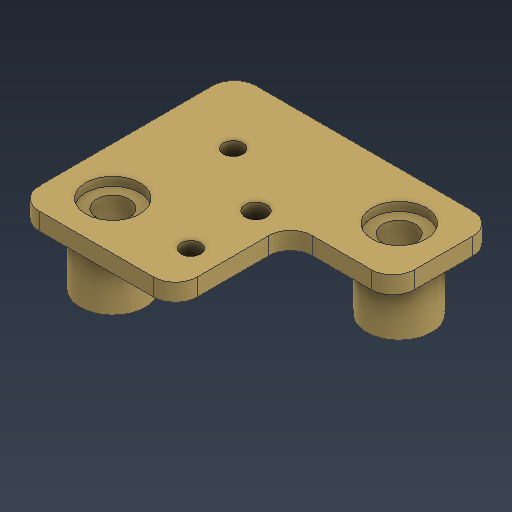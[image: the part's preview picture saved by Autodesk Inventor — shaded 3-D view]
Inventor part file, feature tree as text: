
AUTODESK INVENTOR PART (.ipt)
format: ipt  version: 2021 (Build 250183000, 183)  size: 175,616 bytes
history: native  units: mm
features: extrude x4, other x2, sketch x2
ambient origin geometry x8: Origin, YZ Plane, XZ Plane, XY Plane, X Axis, Y Axis, Z Axis, Center Point
bodies: Body1 (feature_tree)
feature tree (8):
  other  "Chapa Intermediária"
  other  "Sólido1"
  sketch  "Esboço1"  dims[d0=0.8mm d1=0.0mm d2=0.4mm d3=0.0mm]
  extrude  "Extrusão1"  Depth=0.4mm TaperAngle=0.0deg
  extrude  "Extrusão2"  Depth=3.0mm
  extrude  "Extrusão3"  Depth=2.8mm TaperAngle=0.0deg
  extrude  "Extrusão4"  Depth=1.0mm
  sketch  "Esboço2"  dims[d4=3.0mm d5=3.0mm d6=2.8mm d7=0.0mm d9=1.0mm d12=0.9mm d13=2.0mm d14=10.0mm d15=0.0mm]
